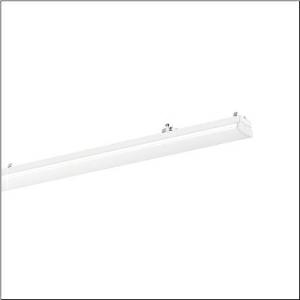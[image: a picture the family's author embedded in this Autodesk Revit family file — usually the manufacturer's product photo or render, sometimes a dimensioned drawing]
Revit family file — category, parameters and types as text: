
# Revit family: licross_21_recessed_opal_mo_52tl1ddn46xg
name_source: partatom
category: Lighting Fixtures
units: mm (PartAtom-declared; Revit-internal decimal feet)

## family parameters
Cut with Voids When Loaded = No
Host = Face
Light Source = No
Part Type = Normal
Room Calculation Point = No
Round Connector Dimension = Use Diameter
Shared = No

## types (1)
- --- (1 x LED, 6320 lm, 36.1 W, 4000K)
    Apparent Load = 36 VA
    CIE Flux Codes = 44 73 91 87 100
    Color Rendering = 80
    Color Temperature = 4000K
    Default Elevation = 1800 mm
    Description = Licross 21 recessed opal MO, luminaire insert, of sheet steel, galvanised, coil coated, white, length: 1.500mm, width: 66mm, height: 67mm, LED rated luminous flux: 6.320lm, light colour: 840, SDCM (Standard Deviation of Colour Matching)MacAdam ≤ 3 SDCM (initial), control gear: DALI 2, with plug, 5-pole, with phase selection, mains connection: 220..240V, AC, 50/60Hz, rated input power: 36W, internal wiring halogen-free, primary optical cover: cover, of PMMA, light emission: direct with ceiling illumination distribution, primary light characteristic: symmetric, protection rating (complete): IP40, insulation class (complete): insulation class I (protective earthing), certification: CE, ENEC, VDE, UKCA, protection symbol: D if used in an environment without relevant dust loads with corresponding accessories, impact resistance: IK06, permissible ambient temperature for indoor applications: -25..+40°C, corresponds to IFS (International Featured Standards) requirements for safety and quality in the food industry, reducing of maximum allowable ambient temperature of 5°C with ceiling mounting, LABS conformity tested according to VDMA 24364:2018-05, The light source and the operating device comply with the requirements of the Ecodesign Regulation (EU) 2019/2020 and are replaceable in accordance with this regulation, packaging unit: 1 piece
    Height = 83 mm
    Lamp = 1 x LED
    Lamp Light Flux = 6320 lm
    Lamp Power = 36.1 W
    Lamp count = 1
    Length = 1500 mm
    Luminous efficacy = 175 lm/W
    Manufacturer = Siteco
    ModVariant = No
    Model = 52TL1DDN46XG
    Mounting Place = Ceiling
    Mounting Type = Pendant
    Number of Poles = 1
    OnlyDefault = Yes
    Power Factor = 1
    Product Name = Licross 21 recessed opal MO
    Product group = luminaire insert | ceiling pendant
    ProductGroupID = 901
    Protection Class = Protection class I
    Protection Degree = IP 40
    RLX_Detail_Level = 1
    RLX_Emergency_Light_Flux = 0 lm
    RLX_Emergency_Type = 0
    RLX_Emergency_Type_DB = No
    RlxData = <blob elided: 26725 chars, md5=cab7641a>
    Socket = socket
    Standby Power = 0 W
    System Light Flux = 6320 lm
    System Power = 36 W
    Type Comments = factory setting: luminous flux: 100 % | dim-lin: 254 | 245 mA
    Type Image = l_1313666.jpg
    URL = http://relux.com
    VarID = @adj_076165
    Voltage = 0 V
    Weight = 0.00 kg
    Width = 76 mm

## geometry (parser evidence)
native form markers: Blend x4, Sweep x13
no freeform markers — native parametric forms only
